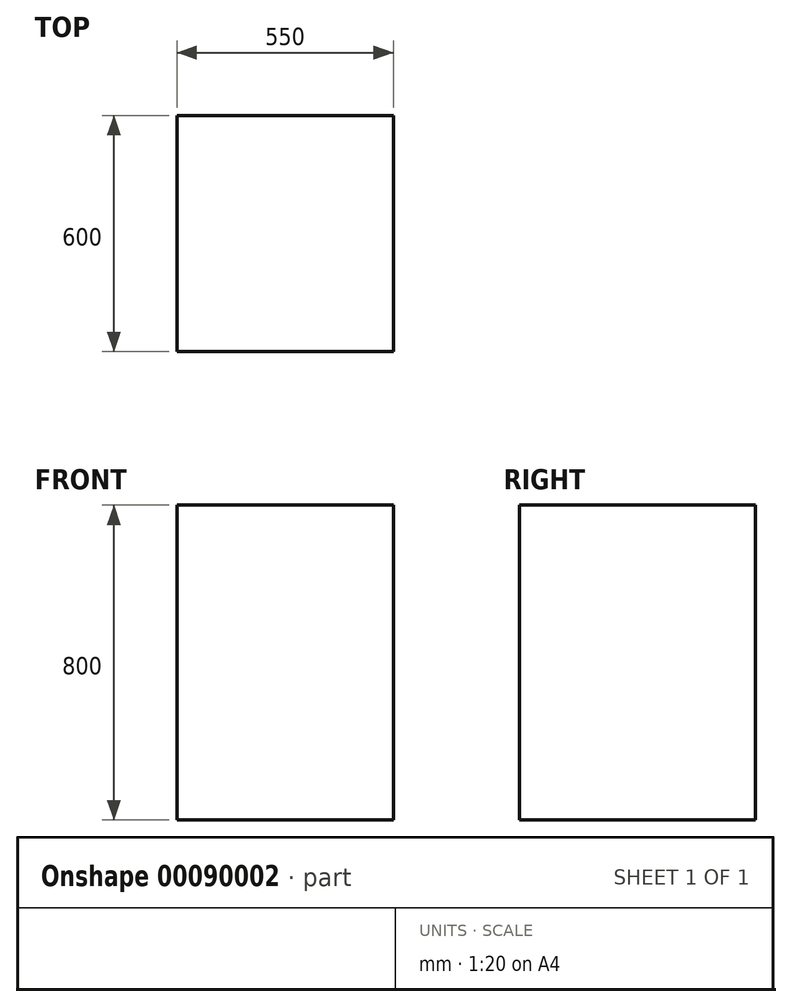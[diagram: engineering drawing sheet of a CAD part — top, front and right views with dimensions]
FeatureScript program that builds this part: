
annotation { "Feature Type Name" : "Feature", "Feature Type Description" : "" }
export const myFeature = defineFeature(function(context is Context, id is Id, definition is map)
    precondition{}
    {
        {
            var Q0;
            Q0=qCreatedBy(makeId("Top.planeOp"),FACE);
            var sketch = newSketch(context, id + "F0", { "sketchPlane" : qUnion([Q0])});
            skLineSegment(sketch, "E0.bottom", {"start": v(0, 0) * mm, "end": v(550, 0) * mm});
            skLineSegment(sketch, "E0.top", {"start": v(0, 600) * mm, "end": v(550, 600) * mm});
            skLineSegment(sketch, "E0.left", {"start": v(0, 0) * mm, "end": v(0, 600) * mm});
            skLineSegment(sketch, "E0.right", {"start": v(550, 0) * mm, "end": v(550, 600) * mm});
            skSolve(sketch);
        }
        {
            var Q0;
            Q0 = qSketchRegion(id + "F0", true);
            var Q1;
            Q1=makeQuery(id+"F0.imprint","IMPRINT",FACE,{"disambiguationData":[TD([[makeQuery(id+"F0.imprint","IMPRINT",EDGE,{"derivedFrom":sQuery(id+"F0.wireOp",EDGE,"E0.bottom")}),1.0]])]});
            extrude(context, id + "F1", {"entities" : qUnion([Q0, Q1]), "depth" : 800 * mm});
        }
    });
